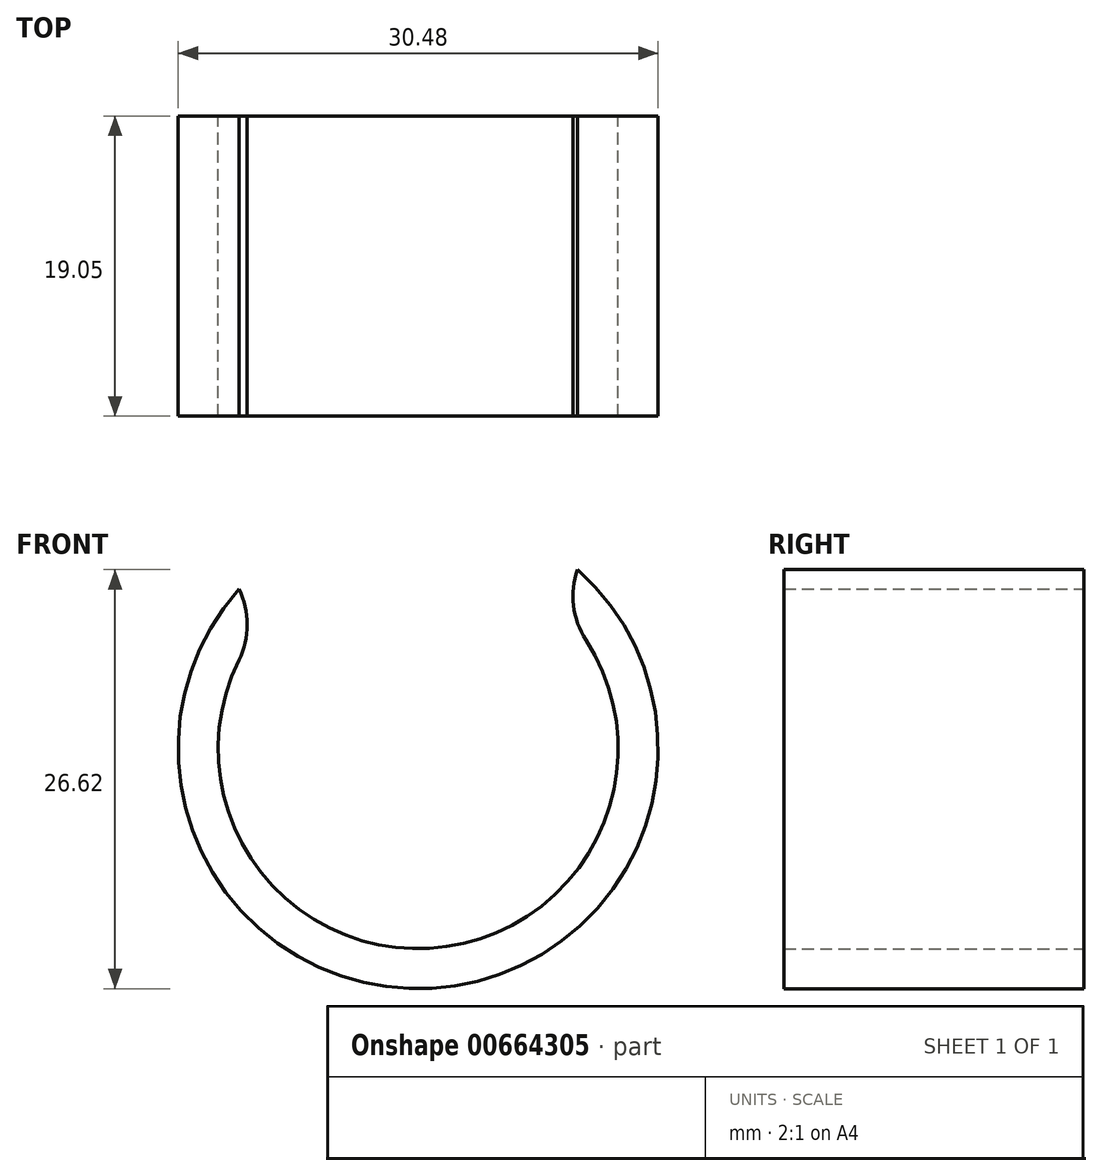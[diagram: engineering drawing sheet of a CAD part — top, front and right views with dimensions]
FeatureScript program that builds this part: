
annotation { "Feature Type Name" : "Feature", "Feature Type Description" : "" }
export const myFeature = defineFeature(function(context is Context, id is Id, definition is map)
    precondition{}
    {
        {
            var Q0;
            Q0=qCreatedBy(makeId("Front.planeOp"),FACE);
            var sketch = newSketch(context, id + "F0", { "sketchPlane" : qUnion([Q0])});
            skCircle(sketch, "E0", {"center": v(0, 0) * mm, "radius": 12.7 * mm});
            skCircle(sketch, "E1", {"center": v(0, 0) * mm, "radius": 15.24 * mm});
            skLineSegment(sketch, "E2", {"start": v(0, 0) * mm, "end": v(-16.77, 14.92) * mm});
            skLineSegment(sketch, "E3", {"start": v(0, 0) * mm, "end": v(12.99, 14.6) * mm});
            skSolve(sketch);
        }
        {
            var Q0;
            {var subQ0=sQuery(id+"F0.wireOp",EDGE,"E2");var subQ1=sQuery(id+"F0.wireOp",EDGE,"E0");var subQ2=makeQuery(id+"F0.imprint","INTERSECT",VERTEX,{"derivedFrom":[subQ1,subQ0]});Q0=makeQuery(id+"F0.imprint","IMPRINT",FACE,{"disambiguationData":[TD([[makeQuery(id+"F0.imprint","IMPRINT",EDGE,{"disambiguationData":[TD([[subQ2,-1.0]])],"derivedFrom":subQ1}),-1.0]])]});}
            extrude(context, id + "F1", {"entities" : qUnion([Q0]), "depth" : 19.05 * mm, "offsetDistance" : 25.4 * mm});
        }
        {
            var Q0;
            Q0=makeQuery(id+"F1.opExtrude","SWEPT_EDGE",EDGE,{"disambiguationData":[OSD([sQuery(id+"F0.wireOp",EDGE,"E0"),sQuery(id+"F0.wireOp",EDGE,"E2")])]});
            var Q1;
            Q1=makeQuery(id+"F1.opExtrude","SWEPT_EDGE",EDGE,{"disambiguationData":[OSD([sQuery(id+"F0.wireOp",EDGE,"E0"),sQuery(id+"F0.wireOp",EDGE,"E3")])]});
            fillet(context, id + "F2", {"entities" : qUnion([Q0, Q1]), "radius" : 5.08 * mm, "tangentPropagation" : true, "allowEdgeOverflow" : false});
        }
    });
